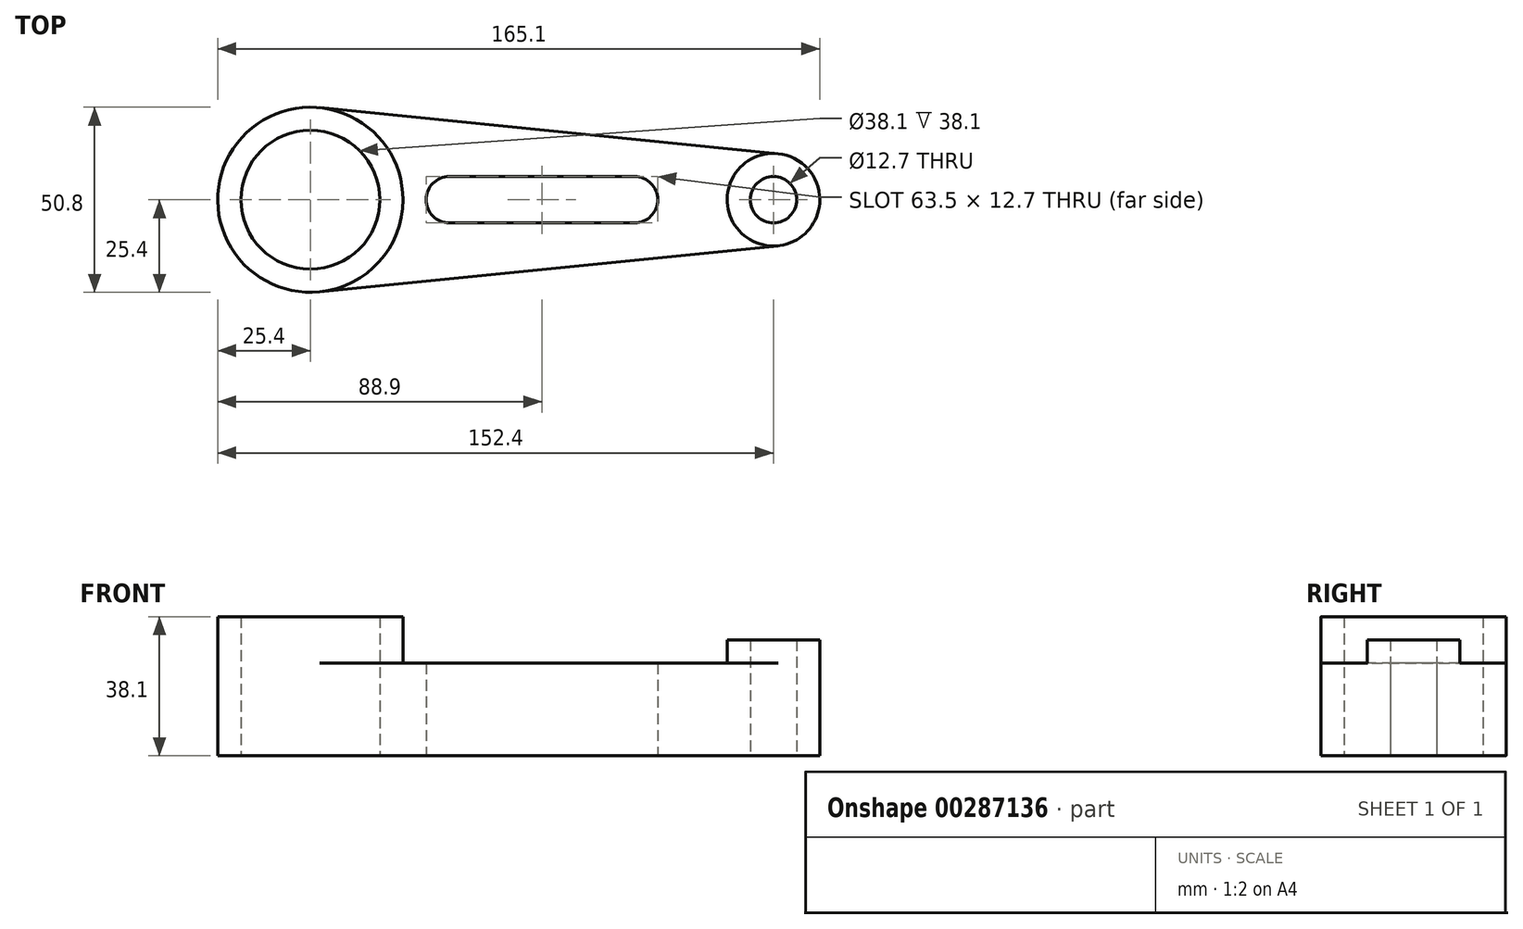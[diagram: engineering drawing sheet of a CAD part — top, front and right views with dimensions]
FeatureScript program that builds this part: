
annotation { "Feature Type Name" : "Feature", "Feature Type Description" : "" }
export const myFeature = defineFeature(function(context is Context, id is Id, definition is map)
    precondition{}
    {
        {
            var Q0;
            Q0=qCreatedBy(makeId("Top.planeOp"),FACE);
            var sketch = newSketch(context, id + "F0", { "sketchPlane" : qUnion([Q0])});
            skArc(sketch, "E0", {"start": v(0, 6.35) * mm, "mid": v(-6.35, 0) * mm, "end": v(0, -6.35) * mm});
            skLineSegment(sketch, "E1", {"start": v(0, -6.35) * mm, "end": v(50.8, -6.35) * mm});
            skArc(sketch, "E2", {"start": v(50.8, -6.35) * mm, "mid": v(57.15, 0) * mm, "end": v(50.8, 6.35) * mm});
            skLineSegment(sketch, "E3", {"start": v(0, 6.35) * mm, "end": v(50.8, 6.35) * mm});
            skCircle(sketch, "E4", {"center": v(88.9, 0) * mm, "radius": 6.35 * mm});
            skCircle(sketch, "E5", {"center": v(88.9, 0) * mm, "radius": 12.7 * mm});
            skCircle(sketch, "E6", {"center": v(-38.1, 0) * mm, "radius": 19.05 * mm});
            skCircle(sketch, "E7", {"center": v(-38.1, 0) * mm, "radius": 25.4 * mm});
            skLineSegment(sketch, "E8", {"start": v(-35.56, 25.27) * mm, "end": v(90.17, 12.64) * mm});
            skLineSegment(sketch, "E9", {"start": v(-35.56, -25.27) * mm, "end": v(90.17, -12.64) * mm});
            skSolve(sketch);
        }
        {
            var Q0;
            Q0=makeQuery(id+"F0.imprint","IMPRINT",FACE,{"disambiguationData":[TD([[makeQuery(id+"F0.imprint","IMPRINT",EDGE,{"derivedFrom":sQuery(id+"F0.wireOp",EDGE,"E6")}),-1.0]])]});
            extrude(context, id + "F1", {"entities" : qUnion([Q0]), "depth" : 38.1 * mm});
        }
        {
            var Q0;
            Q0=makeQuery(id+"F0.imprint","IMPRINT",FACE,{"disambiguationData":[TD([[makeQuery(id+"F0.imprint","IMPRINT",EDGE,{"derivedFrom":sQuery(id+"F0.wireOp",EDGE,"E6")}),-1.0]])]});
            var Q1;
            Q1=makeQuery(id+"F0.imprint","IMPRINT",FACE,{"disambiguationData":[TD([[makeQuery(id+"F0.imprint","IMPRINT",EDGE,{"derivedFrom":sQuery(id+"F0.wireOp",EDGE,"E0")}),-1.0]])]});
            extrude(context, id + "F2", {"entities" : qUnion([Q0, Q1]), "operationType" : NewBodyOperationType.ADD, "depth" : 25.4 * mm});
        }
        {
            var Q0;
            Q0=makeQuery(id+"F0.imprint","IMPRINT",FACE,{"disambiguationData":[TD([[makeQuery(id+"F0.imprint","IMPRINT",EDGE,{"derivedFrom":sQuery(id+"F0.wireOp",EDGE,"E4")}),-1.0]])]});
            extrude(context, id + "F3", {"entities" : qUnion([Q0]), "operationType" : NewBodyOperationType.ADD, "depth" : 31.75 * mm});
        }
    });
